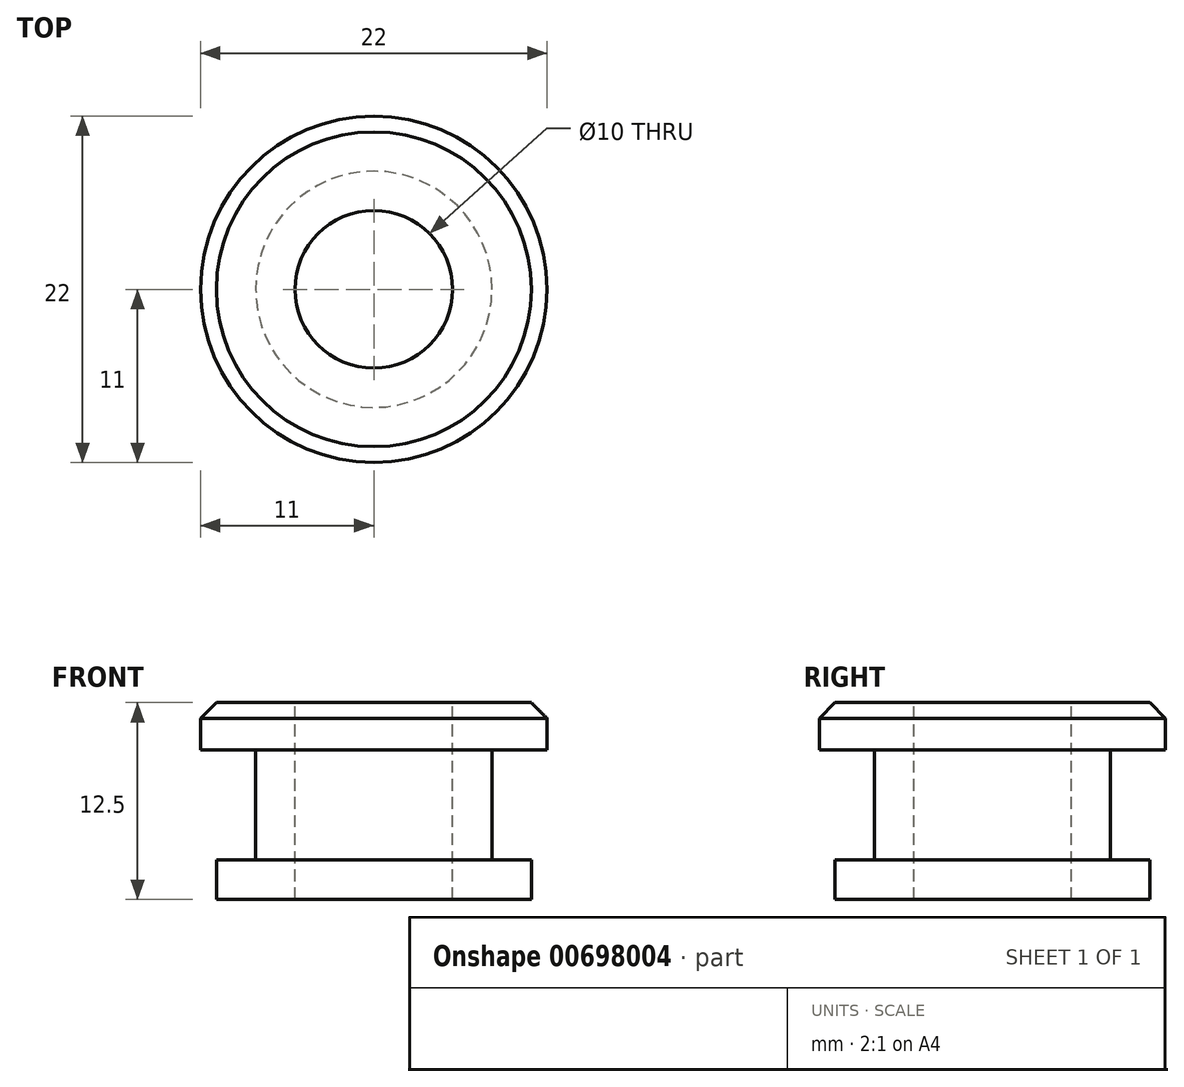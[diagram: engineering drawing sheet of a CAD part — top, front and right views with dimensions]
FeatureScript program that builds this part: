
annotation { "Feature Type Name" : "Feature", "Feature Type Description" : "" }
export const myFeature = defineFeature(function(context is Context, id is Id, definition is map)
    precondition{}
    {
        {
            var Q0;
            Q0=qCreatedBy(makeId("Right.planeOp"),FACE);
            var sketch = newSketch(context, id + "F0", { "sketchPlane" : qUnion([Q0])});
            skLineSegment(sketch, "E0.top", {"start": v(5, -19.45) * mm, "end": v(10, -19.45) * mm});
            skLineSegment(sketch, "E1.bottom", {"start": v(7.5, -9.95) * mm, "end": v(11, -9.95) * mm});
            skLineSegment(sketch, "E1.top", {"start": v(7.5, -16.95) * mm, "end": v(10, -16.95) * mm});
            skLineSegment(sketch, "E1.left", {"start": v(7.5, -9.95) * mm, "end": v(7.5, -16.95) * mm});
            skLineSegment(sketch, "E2", {"start": v(5, -6.95) * mm, "end": v(5, -19.45) * mm});
            skPoint(sketch, "E0.left.start.orphan", {"position": v(0, 10.05) * mm});
            skLineSegment(sketch, "E3.trimOffspring", {"start": v(10, -16.95) * mm, "end": v(10, -19.45) * mm});
            skLineSegment(sketch, "E4", {"start": v(0, 13.73) * mm, "end": v(0, -28.14) * mm, "construction": true});
            skLineSegment(sketch, "E5", {"start": v(5, -6.95) * mm, "end": v(11, -6.95) * mm});
            skLineSegment(sketch, "E6", {"start": v(11, -6.95) * mm, "end": v(11, -9.95) * mm});
            skSolve(sketch);
        }
        {
            var Q0;
            Q0=makeQuery(id+"F0.imprint","IMPRINT",FACE,{"disambiguationData":[TD([[makeQuery(id+"F0.imprint","IMPRINT",EDGE,{"derivedFrom":sQuery(id+"F0.wireOp",EDGE,"E0.top")}),1.0]])]});
            var Q1;
            Q1=sQuery(id+"F0.wireOp",EDGE,"E4");
            revolve(context, id + "F1", {"surfaceOperationType" : NewSurfaceOperationType.NEW, "entities" : qUnion([Q0]), "axis" : qUnion([Q1]), "revolveType" : RevolveType.FULL});
        }
        {
            var Q0;
            Q0=makeQuery(id+"F1.opRevolve","SWEPT_EDGE",EDGE,{"disambiguationData":[OSD([sQuery(id+"F0.wireOp",EDGE,"E5"),sQuery(id+"F0.wireOp",EDGE,"E6")])]});
            chamfer(context, id + "F2", {"entities" : qUnion([Q0]), "width" : 1 * mm, "tangentPropagation" : true});
        }
    });
